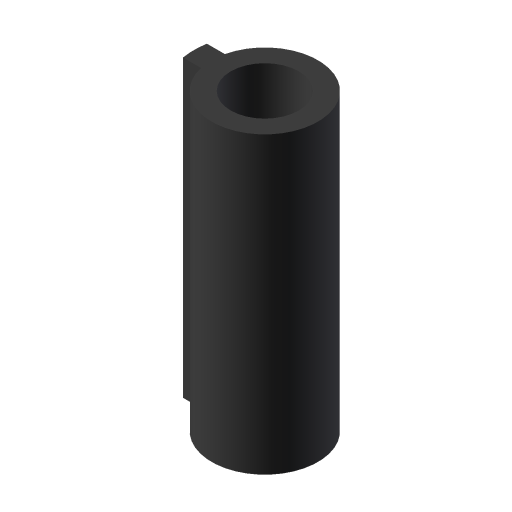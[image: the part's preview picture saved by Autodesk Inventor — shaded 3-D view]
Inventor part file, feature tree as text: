
AUTODESK INVENTOR PART (.ipt)
format: ipt  version: 2023.4 (Build 274418000, 418)  size: 219,136 bytes
history: native  units: in
note: dims shown in document units (in); Inventor stores cm internally (conversion verified against a paired STEP export)
features: extrude x1, sketch x1
ambient origin geometry x8: Origin, YZ Plane, XZ Plane, XY Plane, X Axis, Y Axis, Z Axis, Center Point
bodies: Solid1 (feature_tree)
feature tree (2):
  extrude  "Extrusion1"  TaperAngle=0.0deg  [1 undecoded]
  sketch  "Sketch1"  dims[d0=0.0in d1=0.0in d2=0.3543in d3=0.2283in d4=0.4724in d5=0.0394in d6=0.0394in d7=0.9843in d8=0.0in]
note: 1 required parameter value undecoded (feature->parameter linkage not recoverable at this tier; creation-order binding heuristic only, values carry confidence <= 0.55)
